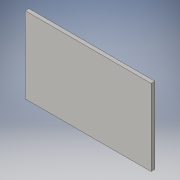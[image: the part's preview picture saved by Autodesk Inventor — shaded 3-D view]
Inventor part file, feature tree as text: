
AUTODESK INVENTOR PART (.ipt)
format: ipt  version: 2016 (Build 200138000, 138)  size: 86,528 bytes
history: native  units: in
note: dims shown in document units (in); Inventor stores cm internally (conversion verified against a paired STEP export)
features: extrude x1, sketch x1
ambient origin geometry x8: Origin, YZ Plane, XZ Plane, XY Plane, X Axis, Y Axis, Z Axis, Center Point
bodies: Solid1 (feature_tree)
feature tree (2):
  extrude  "Extrusion1"  [1 undecoded]
  sketch  "Sketch1"  dims[d3=0.0in]
note: 1 required parameter value undecoded (feature->parameter linkage not recoverable at this tier; creation-order binding heuristic only, values carry confidence <= 0.55)
